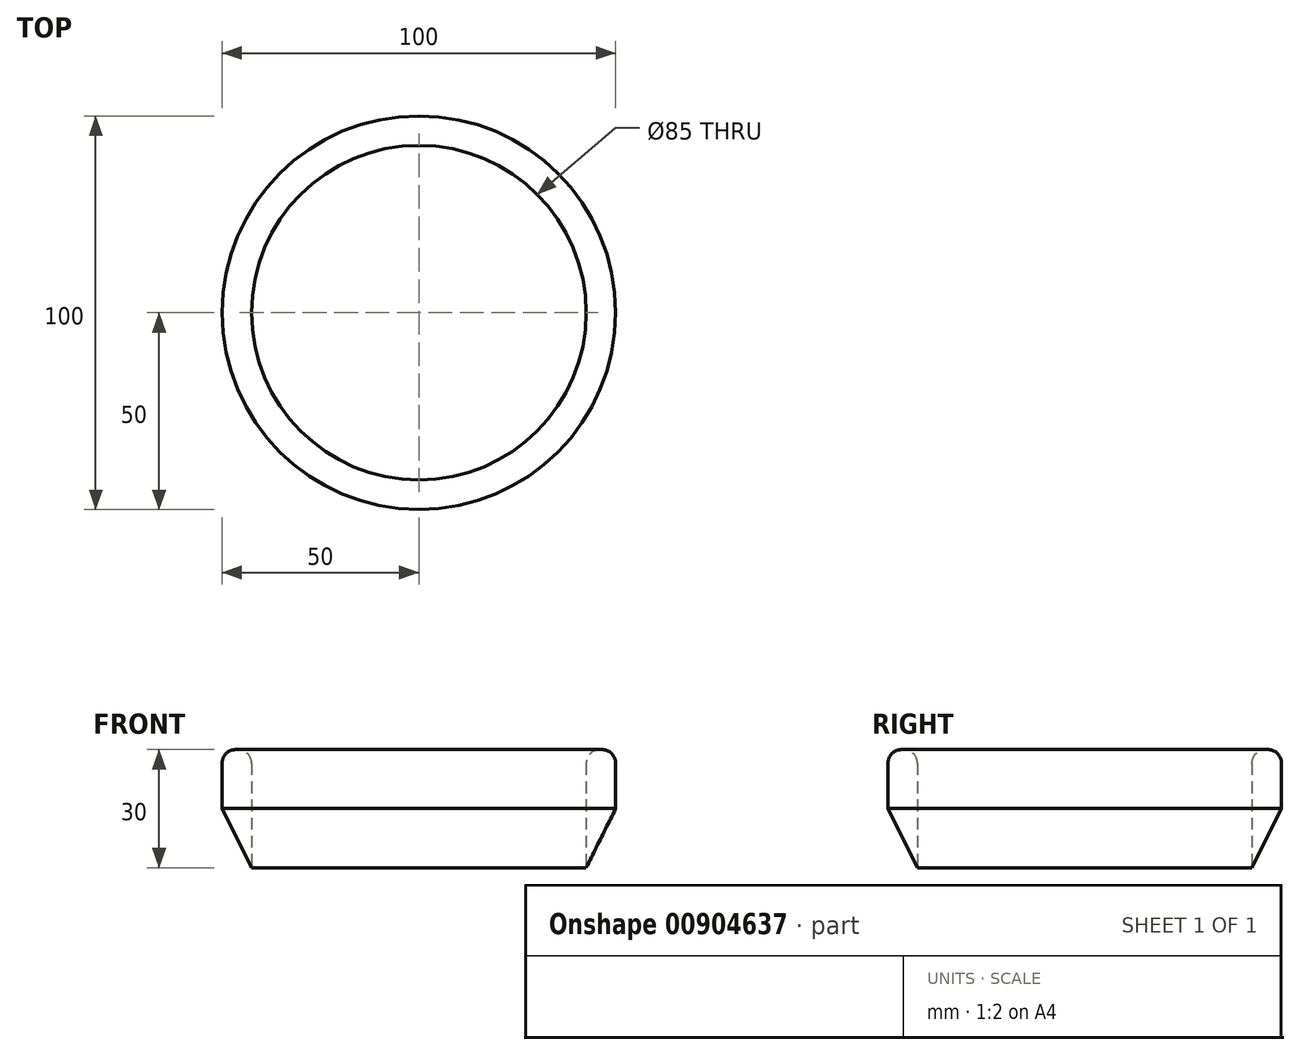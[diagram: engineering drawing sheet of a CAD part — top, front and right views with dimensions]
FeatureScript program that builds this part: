
annotation { "Feature Type Name" : "Feature", "Feature Type Description" : "" }
export const myFeature = defineFeature(function(context is Context, id is Id, definition is map)
    precondition{}
    {
        {
            var Q0;
            Q0=qCreatedBy(makeId("Top.planeOp"),FACE);
            var sketch = newSketch(context, id + "F0", { "sketchPlane" : qUnion([Q0])});
            skCircle(sketch, "E0", {"center": v(0, 0) * mm, "radius": 42.5 * mm});
            skCircle(sketch, "E1", {"center": v(0, 0) * mm, "radius": 50 * mm});
            skSolve(sketch);
        }
        {
            var Q0;
            Q0=makeQuery(id+"F0.imprint","IMPRINT",FACE,{"disambiguationData":[TD([[makeQuery(id+"F0.imprint","IMPRINT",EDGE,{"derivedFrom":sQuery(id+"F0.wireOp",EDGE,"E0")}),-1.0]])]});
            extrude(context, id + "F1", {"entities" : qUnion([Q0]), "depth" : 30 * mm, "offsetDistance" : 25 * mm, "symmetric" : true});
        }
        {
            var Q0;
            Q0=makeQuery(id+"F1.opExtrude","CAP_EDGE",EDGE,{"disambiguationData":[OSD([sQuery(id+"F0.wireOp",EDGE,"E1")])],"isStart":true});
            chamfer(context, id + "F2", {"entities" : qUnion([Q0]), "chamferType" : ChamferType.TWO_OFFSETS, "width1" : 15 * mm, "oppositeDirection" : false, "width2" : 7.5 * mm, "tangentPropagation" : true});
        }
        {
            var Q0;
            Q0=makeQuery(id+"F1.opExtrude","CAP_EDGE",EDGE,{"disambiguationData":[OSD([sQuery(id+"F0.wireOp",EDGE,"E1")])],"isStart":false});
            var Q1;
            Q1=makeQuery(id+"F1.opExtrude","CAP_EDGE",EDGE,{"disambiguationData":[OSD([sQuery(id+"F0.wireOp",EDGE,"E0")])],"isStart":false});
            fillet(context, id + "F3", {"entities" : qUnion([Q0, Q1]), "radius" : 3.5 * mm, "tangentPropagation" : true, "allowEdgeOverflow" : false});
        }
    });
